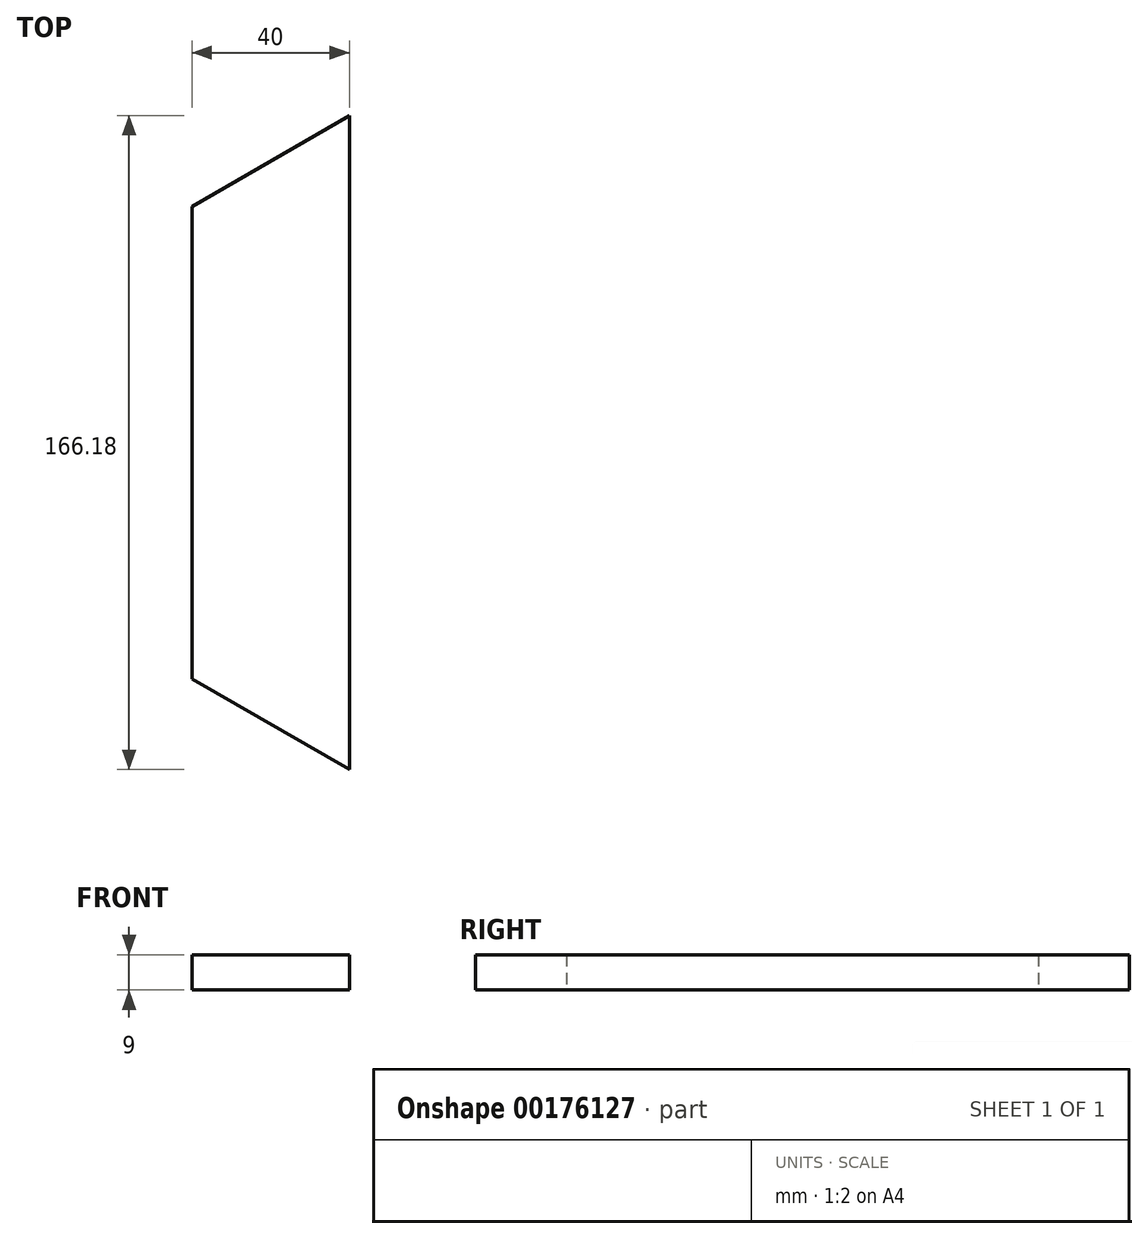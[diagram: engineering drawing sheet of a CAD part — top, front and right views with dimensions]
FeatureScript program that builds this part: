
annotation { "Feature Type Name" : "Feature", "Feature Type Description" : "" }
export const myFeature = defineFeature(function(context is Context, id is Id, definition is map)
    precondition{}
    {
        {
            var Q0;
            Q0=qCreatedBy(makeId("Top.planeOp"),FACE);
            var sketch = newSketch(context, id + "F0", { "sketchPlane" : qUnion([Q0])});
            skLineSegment(sketch, "E0", {"start": v(0, 0) * mm, "end": v(0, 120) * mm});
            skLineSegment(sketch, "E1", {"start": v(0, 120) * mm, "end": v(40, 143.1) * mm});
            skLineSegment(sketch, "E2", {"start": v(40, 143.1) * mm, "end": v(40, -23.1) * mm});
            skLineSegment(sketch, "E3", {"start": v(40, -23.1) * mm, "end": v(0, 0) * mm});
            skSolve(sketch);
        }
        {
            var Q0;
            Q0 = qSketchRegion(id + "F0", true);
            extrude(context, id + "F1", {"entities" : qUnion([Q0]), "depth" : 9 * mm});
        }
    });
